# Revit family: Access_Door-Cabinet-Best Access Doors-Box-BA-VBW
name_source: partatom
category: Specialty Equipment
revit_build: Autodesk Revit 2017 (Build: 20160225_1515(x64)
units: mm (PartAtom-declared; Revit-internal decimal feet)

## family parameters
Cut with Voids When Loaded = No
Host = Face
OmniClass Number = 23.30.10.27.17
Part Type = Normal
Room Calculation Point = No
Round Connector Dimension = Use Diameter
Shared = No

## types (4) — shared parameters
4in Frame Depth = No
6in Frame Depth = Yes
Assembly Code = C1020700
Construction Material = Metal - Best Access Doors - Aluminum
Default Elevation = 0"
Description = Cabinets and Valve Boxes
Finish = Metal - Best Access Doors - Powder Coated White
Frame Depth = 6"
Glass = Glass - Best Access Doors - Plexiglass
Manufacturer = Best Access Doors
Max Area = 900 in²
Model = BA-VBW
Product data url = https://bimobject.com
URL = http://www.bestaccessdoors.com

## per-type parameters (varying)
| type | Area | Door Height | Door Width | Frame Height | Frame Width | Height Calc | Width Calc | Window Height | Window Width |
| Custom | 900 in² | 30" | 30" | 29 1/8" | 29 1/8" | 30" | 30" | 8" | 8" |
| 8 1/4 x 8 1/4 | 68.06 in² | 8 1/4" | 8 1/4" | 7 3/8" | 7 3/8" | 8 1/4" | 8 1/4" | 3" | 3" |
| 12 x 12 | 144 in² | 12" | 12" | 11 1/8" | 11 1/8" | 12" | 12" | 5" | 5" |
| 16 x 16 | 256 in² | 16" | 16" | 15 1/8" | 15 1/8" | 16" | 16" | 8" | 8" |

## geometry (parser evidence)
native form markers: Blend x4, Sweep x11
no freeform markers — native parametric forms only
